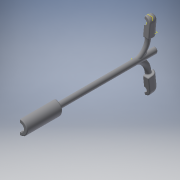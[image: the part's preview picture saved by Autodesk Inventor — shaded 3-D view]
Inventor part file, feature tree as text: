
AUTODESK INVENTOR PART (.ipt)
format: ipt  version: 2018 (Build 220112000, 112)  size: 582,656 bytes
history: native  units: mm
features: sketch x11, extrude x9, fillet x6, plane x3, projected_geometry x3, revolve x1, sweep x1, mirror x1
ambient origin geometry x8: Origin, YZ Plane, XZ Plane, XY Plane, X Axis, Y Axis, Z Axis, Center Point
bodies: Solid1 (feature_tree)
feature tree (35):
  revolve  "Revolution1"  [1 undecoded]
  fillet  "Fillet1"  Radius=8.0mm
  fillet  "Fillet2"  Radius=40.0mm
  fillet  "Fillet3"  [1 undecoded]
  plane  "Work Plane1"
  sweep  "Sweep1"
  extrude  "Extrusion2"  Depth=1.0mm
  fillet  "Fillet4"  Radius=1.5mm
  fillet  "Fillet5"  Radius=1.0mm
  extrude  "Extrusion3"  Depth=4.0mm
  extrude  "Extrusion4"  Depth=2.0mm
  extrude  "Extrusion5"  Depth=1.0mm
  extrude  "Extrusion6"  Depth=18.0mm
  extrude  "Extrusion7"  Depth=16.0mm
  plane  "Work Plane3"
  extrude  "Extrusion8"  Depth=12.0mm
  extrude  "Extrusion9"  Depth=6.0mm
  plane  "Work Plane4"
  extrude  "Extrusion10"  Depth=20.0mm TaperAngle=0.0deg
  fillet  "Fillet6"  Radius=6.0mm
  mirror  "Mirror2"
  sketch  "Sketch6"  dims[d0=150.0mm d1=3.5mm d3=8.0mm d4=40.0mm d5=90.0deg]
  sketch  "Sketch8"  dims[d20=1.5mm d21=1.5mm]
  sketch  "Sketch9"  dims[d22=1.5mm d23=1.0mm d24=1.5mm d25=1.0mm]
  projected_geometry  "Projected Loop3"
  sketch  "Sketch10"  dims[d26=1.5mm d27=4.0mm]
  projected_geometry  "Projected Loop4"
  sketch  "Sketch11"  dims[d29=9.0mm d30=2.0mm]
  sketch  "Sketch12"  dims[d31=1.0mm d32=1.0mm]
  sketch  "Sketch13"  dims[d33=-23.0mm d38=18.0mm]
  sketch  "Sketch14"  dims[d39=18.0mm d40=16.0mm]
  sketch  "Sketch15"  dims[d41=0.0mm d42=0.0mm d43=12.0mm]
  projected_geometry  "Projected Loop5"
  sketch  "Sketch16"  dims[d44=5.0mm d45=6.0mm]
  sketch  "Sketch17"  dims[d46=6.0mm d47=20.0mm d48=0.0mm d49=6.0mm d50=1.0mm d51=4.0mm d52=5.5mm d53=8.0mm d54=0.0mm d55=10.0mm d56=0.0mm d57=50.0mm d58=0.0mm d59=1.5mm d60=0.0mm d61=6.0mm d62=15.0mm d63=0.0mm d64=-3.0mm d65=6.5mm d66=1.1mm d67=0.0mm d68=10.0mm d69=0.0mm d70=-3.0mm d71=10.0mm d72=0.0mm d73=0.5mm d74=8.25mm]
note: 2 required parameter values undecoded (feature->parameter linkage not recoverable at this tier; creation-order binding heuristic only, values carry confidence <= 0.55)